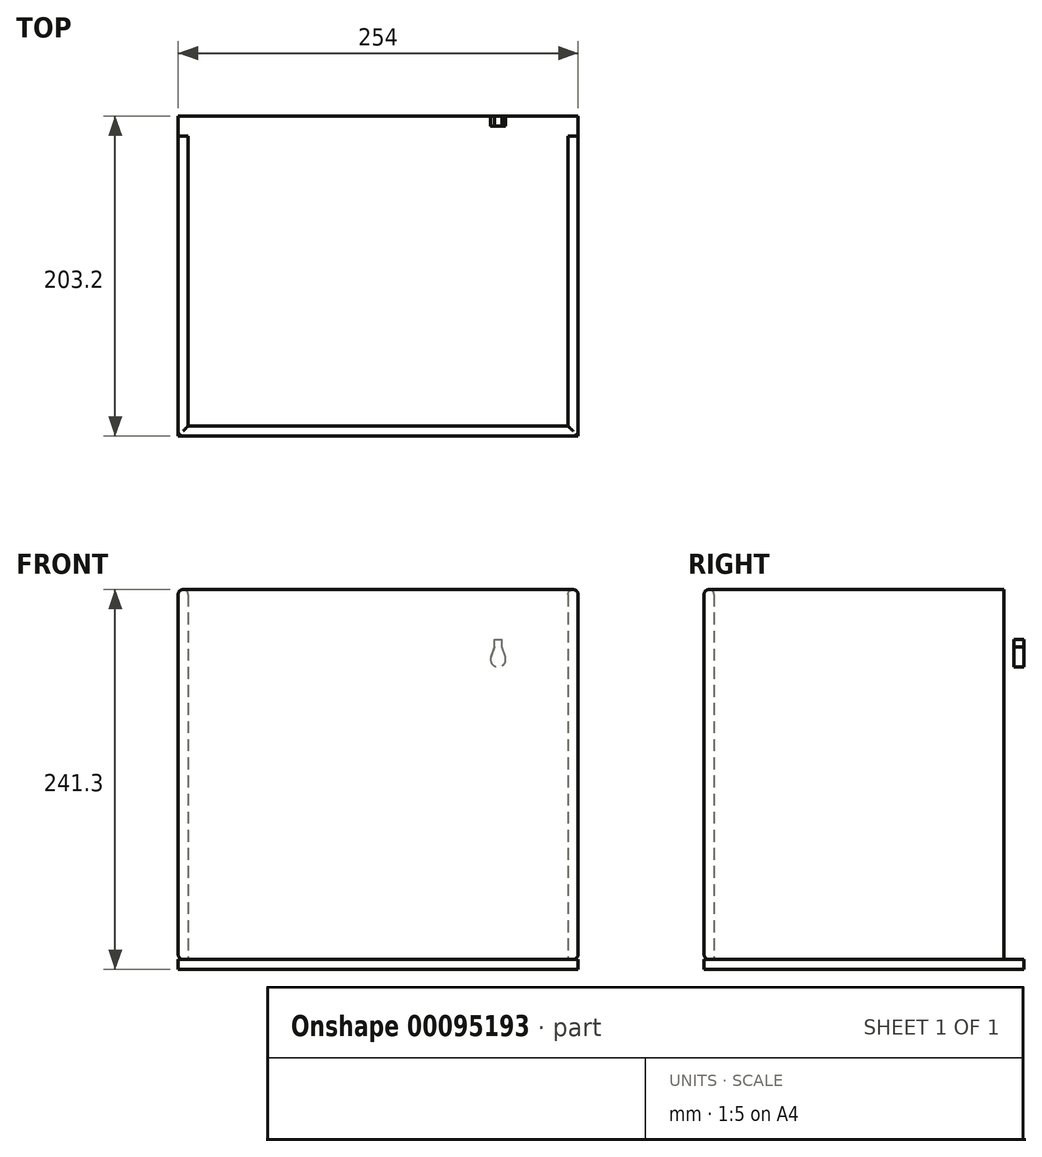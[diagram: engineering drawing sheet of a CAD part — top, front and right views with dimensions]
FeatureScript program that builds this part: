
annotation { "Feature Type Name" : "Feature", "Feature Type Description" : "" }
export const myFeature = defineFeature(function(context is Context, id is Id, definition is map)
    precondition{}
    {
        {
            var Q0;
            Q0=qCreatedBy(makeId("Top.planeOp"),FACE);
            var sketch = newSketch(context, id + "F0", { "sketchPlane" : qUnion([Q0])});
            skLineSegment(sketch, "E0.bottom", {"start": v(127, -101.6) * mm, "end": v(-127, -101.6) * mm});
            skLineSegment(sketch, "E0.top", {"start": v(127, 101.6) * mm, "end": v(-127, 101.6) * mm});
            skLineSegment(sketch, "E0.left", {"start": v(127, -101.6) * mm, "end": v(127, 101.6) * mm});
            skLineSegment(sketch, "E0.right", {"start": v(-127, -101.6) * mm, "end": v(-127, 101.6) * mm});
            skPoint(sketch, "E0.middle", {"position": v(0, 0) * mm});
            skLineSegment(sketch, "E1.0", {"start": v(120.65, 95.25) * mm, "end": v(-120.65, 95.25) * mm});
            skLineSegment(sketch, "E1.1", {"start": v(120.65, -95.25) * mm, "end": v(120.65, 95.25) * mm});
            skLineSegment(sketch, "E1.2", {"start": v(120.65, -95.25) * mm, "end": v(-120.65, -95.25) * mm});
            skLineSegment(sketch, "E1.3", {"start": v(-120.65, -95.25) * mm, "end": v(-120.65, 95.25) * mm});
            skSolve(sketch);
        }
        {
            var Q0;
            Q0=makeQuery(id+"F0.imprint","IMPRINT",FACE,{"disambiguationData":[TD([[makeQuery(id+"F0.imprint","IMPRINT",EDGE,{"derivedFrom":sQuery(id+"F0.wireOp",EDGE,"E0.bottom")}),-1.0]])]});
            extrude(context, id + "F1", {"entities" : qUnion([Q0]), "depth" : 234.95 * mm});
        }
        {
            var Q0;
            Q0=makeQuery(id+"F0.imprint","IMPRINT",FACE,{"disambiguationData":[TD([[makeQuery(id+"F0.imprint","IMPRINT",EDGE,{"derivedFrom":sQuery(id+"F0.wireOp",EDGE,"E1.0")}),1.0]])]});
            var Q1;
            Q1=makeQuery(id+"F0.imprint","IMPRINT",FACE,{"disambiguationData":[TD([[makeQuery(id+"F0.imprint","IMPRINT",EDGE,{"derivedFrom":sQuery(id+"F0.wireOp",EDGE,"E0.bottom")}),-1.0]])]});
            extrude(context, id + "F2", {"entities" : qUnion([Q0, Q1]), "oppositeDirection" : true, "depth" : 6.35 * mm});
        }
        {
            var Q0;
            Q0=makeQuery(id+"F1.opExtrude","SWEPT_FACE",FACE,{"disambiguationData":[OSD([sQuery(id+"F0.wireOp",EDGE,"E0.top")])]});
            var sketch = newSketch(context, id + "F3", { "sketchPlane" : qUnion([Q0])});
            skLineSegment(sketch, "E2", {"start": v(0, 234.95) * mm, "end": v(0, 184.15) * mm, "construction": true});
            skPoint(sketch, "E2.endSnap0", {"position": v(0, 234.95) * mm});
            skLineSegment(sketch, "E3", {"start": v(-76.2, 184.15) * mm, "end": v(76.2, 184.15) * mm, "construction": true});
            skLineSegment(sketch, "E4", {"start": v(-76.2, 184.15) * mm, "end": v(-76.2, 171.45) * mm, "construction": true});
            skArc(sketch, "E5.MirrorCS", {"start": v(-71.68, 192) * mm, "mid": v(-76.2, 185.74) * mm, "end": v(-80.72, 192) * mm});
            skLineSegment(sketch, "E6.MirrorCS", {"start": v(-78.58, 198.44) * mm, "end": v(-80.72, 192) * mm});
            skLineSegment(sketch, "E7.MirrorCS", {"start": v(-73.82, 198.44) * mm, "end": v(-71.68, 192) * mm});
            skLineSegment(sketch, "E8.MirrorCS", {"start": v(-73.82, 203.2) * mm, "end": v(-73.82, 198.44) * mm});
            skLineSegment(sketch, "E9.MirrorCS", {"start": v(-78.58, 203.2) * mm, "end": v(-73.82, 203.2) * mm});
            skLineSegment(sketch, "E10.MirrorCS", {"start": v(-78.58, 203.2) * mm, "end": v(-78.58, 198.44) * mm});
            skArc(sketch, "E11.MirrorCS", {"start": v(71.68, 192) * mm, "mid": v(76.2, 185.74) * mm, "end": v(80.72, 192) * mm});
            skLineSegment(sketch, "E12.MirrorCS", {"start": v(78.58, 198.44) * mm, "end": v(80.72, 192) * mm});
            skLineSegment(sketch, "E13.MirrorCS", {"start": v(73.82, 198.44) * mm, "end": v(71.68, 192) * mm});
            skLineSegment(sketch, "E14.MirrorCS", {"start": v(73.82, 203.2) * mm, "end": v(73.82, 198.44) * mm});
            skLineSegment(sketch, "E15.MirrorCS", {"start": v(78.58, 203.2) * mm, "end": v(73.82, 203.2) * mm});
            skLineSegment(sketch, "E16.MirrorCS", {"start": v(78.58, 203.2) * mm, "end": v(78.58, 198.44) * mm});
            skSolve(sketch);
        }
        {
            var Q0;
            Q0=makeQuery(id+"F3.imprint","IMPRINT",FACE,{"disambiguationData":[TD([[makeQuery(id+"F3.imprint","IMPRINT",EDGE,{"derivedFrom":sQuery(id+"F3.wireOp",EDGE,"E5.MirrorCS")}),-1.0]])]});
            var Q1;
            Q1=makeQuery(id+"F3.imprint","IMPRINT",FACE,{"disambiguationData":[TD([[makeQuery(id+"F3.imprint","IMPRINT",EDGE,{"derivedFrom":sQuery(id+"F3.wireOp",EDGE,"E11.MirrorCS")}),1.0]])]});
            extrude(context, id + "F4", {"entities" : qUnion([Q0, Q1]), "operationType" : NewBodyOperationType.REMOVE, "oppositeDirection" : true, "depth" : 12.7 * mm});
        }
        {
            var Q0;
            Q0=makeQuery(id+"F1.opExtrude","SWEPT_EDGE",EDGE,{"disambiguationData":[OSD([sQuery(id+"F0.wireOp",EDGE,"E0.top"),sQuery(id+"F0.wireOp",EDGE,"E0.left")])]});
            var Q1;
            Q1=makeQuery(id+"F1.opExtrude","SWEPT_EDGE",EDGE,{"disambiguationData":[OSD([sQuery(id+"F0.wireOp",EDGE,"E0.bottom"),sQuery(id+"F0.wireOp",EDGE,"E0.left")])]});
            var Q2;
            Q2=makeQuery(id+"F1.opExtrude","CAP_EDGE",EDGE,{"disambiguationData":[OSD([sQuery(id+"F0.wireOp",EDGE,"E0.left")])],"isStart":true});
            var Q3;
            Q3=makeQuery(id+"F1.opExtrude","CAP_EDGE",EDGE,{"disambiguationData":[OSD([sQuery(id+"F0.wireOp",EDGE,"E0.top")])],"isStart":true});
            var Q4;
            Q4=makeQuery(id+"F1.opExtrude","SWEPT_EDGE",EDGE,{"disambiguationData":[OSD([sQuery(id+"F0.wireOp",EDGE,"E0.top"),sQuery(id+"F0.wireOp",EDGE,"E0.right")])]});
            var Q5;
            Q5=makeQuery(id+"F1.opExtrude","SWEPT_EDGE",EDGE,{"disambiguationData":[OSD([sQuery(id+"F0.wireOp",EDGE,"E0.bottom"),sQuery(id+"F0.wireOp",EDGE,"E0.right")])]});
            var Q6;
            Q6=makeQuery(id+"F1.opExtrude","CAP_EDGE",EDGE,{"disambiguationData":[OSD([sQuery(id+"F0.wireOp",EDGE,"E0.bottom")])],"isStart":true});
            var Q7;
            Q7=makeQuery(id+"F1.opExtrude","CAP_EDGE",EDGE,{"disambiguationData":[OSD([sQuery(id+"F0.wireOp",EDGE,"E0.right")])],"isStart":true});
            var Q8;
            Q8=makeQuery(id+"F1.opExtrude","CAP_EDGE",EDGE,{"disambiguationData":[OSD([sQuery(id+"F0.wireOp",EDGE,"E0.top")])],"isStart":false});
            var Q9;
            Q9=makeQuery(id+"F1.opExtrude","CAP_EDGE",EDGE,{"disambiguationData":[OSD([sQuery(id+"F0.wireOp",EDGE,"E0.left")])],"isStart":false});
            var Q10;
            Q10=makeQuery(id+"F1.opExtrude","CAP_EDGE",EDGE,{"disambiguationData":[OSD([sQuery(id+"F0.wireOp",EDGE,"E0.right")])],"isStart":false});
            var Q11;
            Q11=makeQuery(id+"F1.opExtrude","CAP_EDGE",EDGE,{"disambiguationData":[OSD([sQuery(id+"F0.wireOp",EDGE,"E0.bottom")])],"isStart":false});
            var Q12;
            Q12=makeQuery(id+"F1.opExtrude","CAP_EDGE",EDGE,{"disambiguationData":[OSD([sQuery(id+"F0.wireOp",EDGE,"E1.2")])],"isStart":false});
            var Q13;
            Q13=makeQuery(id+"F1.opExtrude","CAP_EDGE",EDGE,{"disambiguationData":[OSD([sQuery(id+"F0.wireOp",EDGE,"E1.1")])],"isStart":false});
            var Q14;
            Q14=makeQuery(id+"F1.opExtrude","CAP_EDGE",EDGE,{"disambiguationData":[OSD([sQuery(id+"F0.wireOp",EDGE,"E1.3")])],"isStart":false});
            var Q15;
            Q15=makeQuery(id+"F1.opExtrude","CAP_EDGE",EDGE,{"disambiguationData":[OSD([sQuery(id+"F0.wireOp",EDGE,"E1.0")])],"isStart":false});
            fillet(context, id + "F5", {"entities" : qUnion([Q0, Q1, Q2, Q3, Q4, Q5, Q6, Q7, Q8, Q9, Q10, Q11, Q12, Q13, Q14, Q15]), "radius" : 3.17 * mm, "tangentPropagation" : true, "allowEdgeOverflow" : false});
        }
    });
